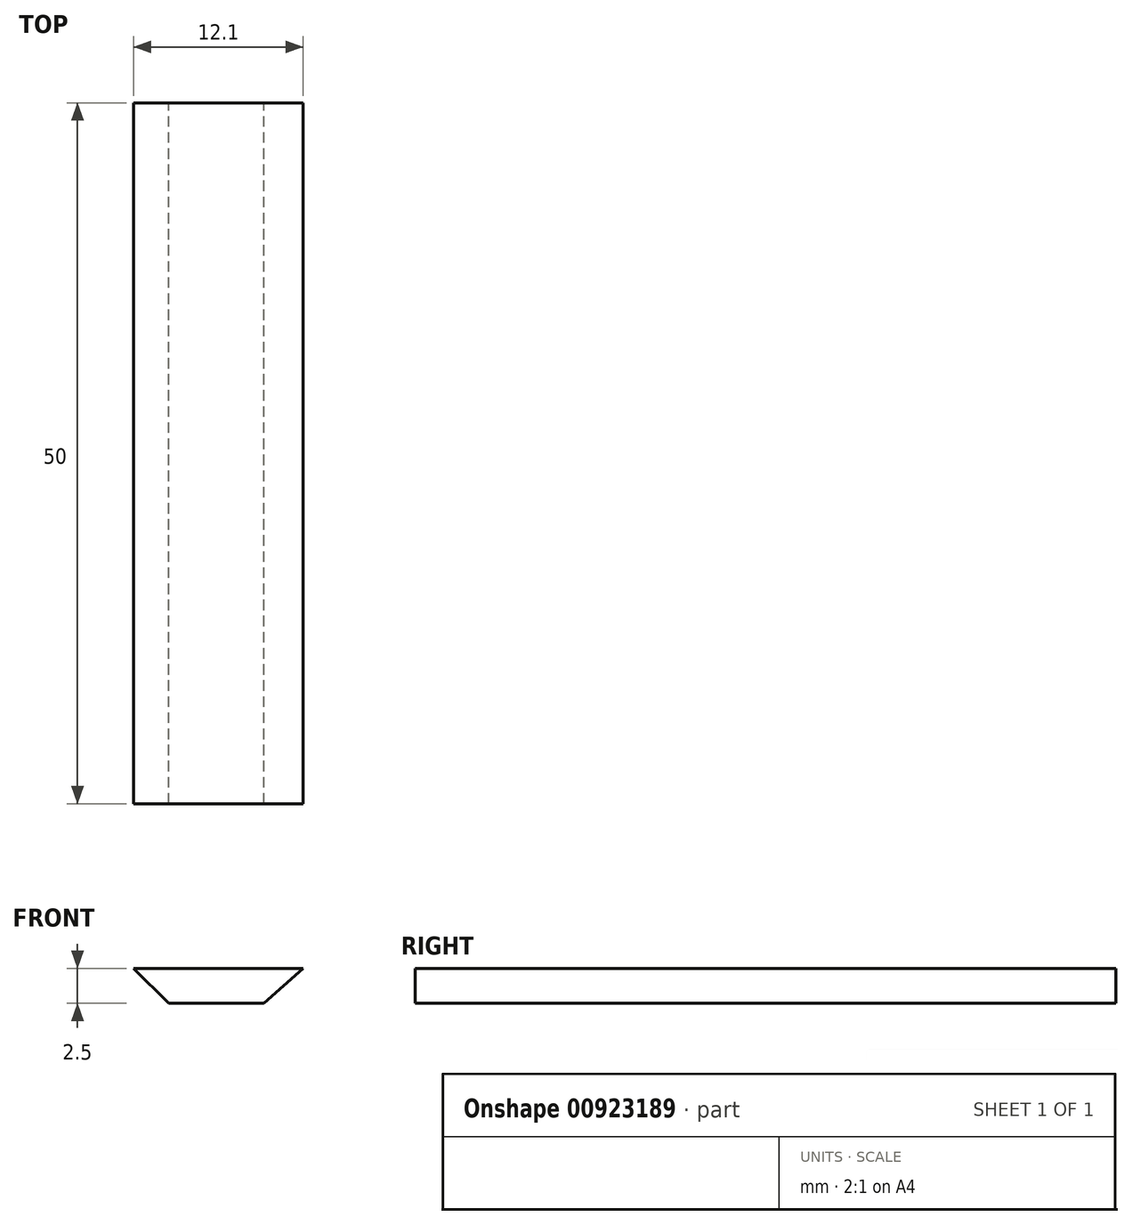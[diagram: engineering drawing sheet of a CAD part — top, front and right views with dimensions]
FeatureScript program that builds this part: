
annotation { "Feature Type Name" : "Feature", "Feature Type Description" : "" }
export const myFeature = defineFeature(function(context is Context, id is Id, definition is map)
    precondition{}
    {
        {
            var Q0;
            Q0=qCreatedBy(makeId("Front.planeOp"),FACE);
            var sketch = newSketch(context, id + "F0", { "sketchPlane" : qUnion([Q0])});
            skLineSegment(sketch, "E0", {"start": v(-3.96, 0) * mm, "end": v(-6.48, 2.5) * mm});
            skLineSegment(sketch, "E1", {"start": v(-6.48, 2.5) * mm, "end": v(5.62, 2.5) * mm});
            skLineSegment(sketch, "E2", {"start": v(5.62, 2.5) * mm, "end": v(2.84, 0) * mm});
            skLineSegment(sketch, "E3", {"start": v(2.84, 0) * mm, "end": v(-3.96, 0) * mm});
            skSolve(sketch);
        }
        {
            var Q0;
            Q0=makeQuery(id+"F0.imprint","IMPRINT",FACE,{"disambiguationData":[TD([[makeQuery(id+"F0.imprint","IMPRINT",EDGE,{"derivedFrom":sQuery(id+"F0.wireOp",EDGE,"E0")}),-1.0]])]});
            extrude(context, id + "F1", {"entities" : qUnion([Q0]), "depth" : 50 * mm, "offsetDistance" : 25 * mm});
        }
    });
